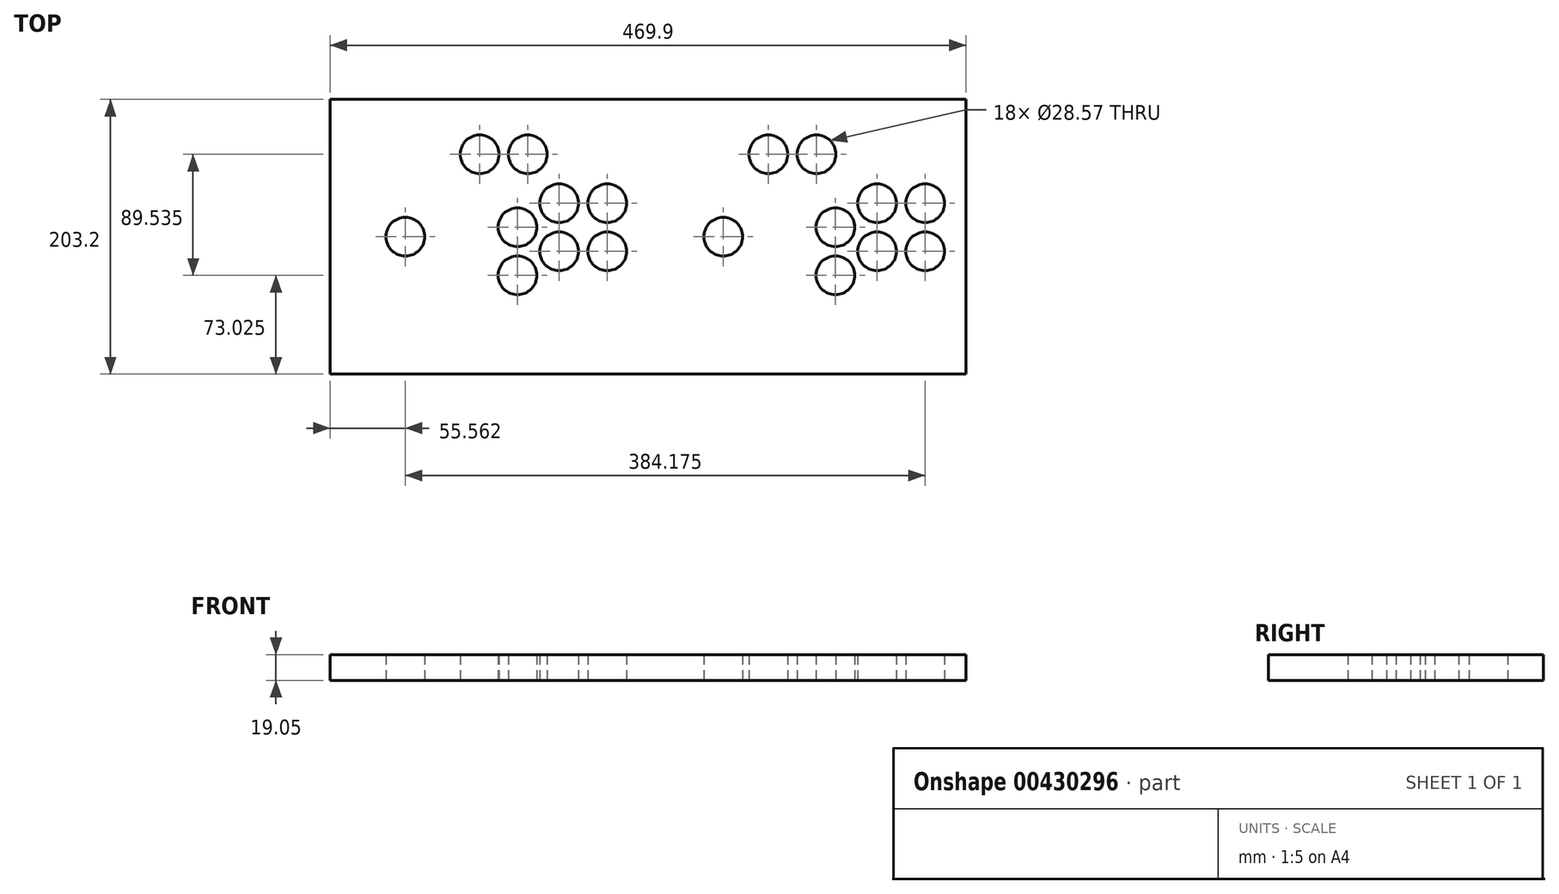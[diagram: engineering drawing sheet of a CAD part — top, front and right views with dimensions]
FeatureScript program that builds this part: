
annotation { "Feature Type Name" : "Feature", "Feature Type Description" : "" }
export const myFeature = defineFeature(function(context is Context, id is Id, definition is map)
    precondition{}
    {
        {
            var Q0;
            Q0=qCreatedBy(makeId("Top.planeOp"),FACE);
            var sketch = newSketch(context, id + "F0", { "sketchPlane" : qUnion([Q0])});
            skCircle(sketch, "E0", {"center": v(-179.39, 0) * mm, "radius": 14.29 * mm});
            skLineSegment(sketch, "E1.bottom", {"start": v(-219.08, -44.45) * mm, "end": v(-139.7, -44.45) * mm});
            skLineSegment(sketch, "E1.top", {"start": v(-219.08, 44.45) * mm, "end": v(-139.7, 44.45) * mm});
            skLineSegment(sketch, "E1.left", {"start": v(-219.08, -44.45) * mm, "end": v(-219.08, 44.45) * mm});
            skLineSegment(sketch, "E1.right", {"start": v(-139.7, -44.45) * mm, "end": v(-139.7, 44.45) * mm});
            skPoint(sketch, "E2.positionSnap0", {"position": v(-139.7, 0) * mm});
            skPoint(sketch, "E2.positionSnap1", {"position": v(-179.39, -44.45) * mm});
            skCircle(sketch, "E3", {"center": v(-96.52, -28.58) * mm, "radius": 14.29 * mm});
            skCircle(sketch, "E4", {"center": v(-96.52, 6.98) * mm, "radius": 14.29 * mm});
            skCircle(sketch, "E5", {"center": v(-30.16, 24.76) * mm, "radius": 14.29 * mm});
            skCircle(sketch, "E6", {"center": v(-65.72, -10.8) * mm, "radius": 14.29 * mm});
            skCircle(sketch, "E7", {"center": v(-65.72, 24.76) * mm, "radius": 14.29 * mm});
            skCircle(sketch, "E8", {"center": v(-30.16, -10.8) * mm, "radius": 14.29 * mm});
            skLineSegment(sketch, "E9", {"start": v(-96.52, -28.58) * mm, "end": v(-96.52, 0) * mm, "construction": true});
            skLineSegment(sketch, "E10", {"start": v(-179.39, 0) * mm, "end": v(-96.52, 0) * mm, "construction": true});
            skLineSegment(sketch, "E11", {"start": v(-96.52, -28.58) * mm, "end": v(-96.52, 6.98) * mm, "construction": true});
            skLineSegment(sketch, "E12", {"start": v(-96.52, 6.98) * mm, "end": v(-65.72, 24.76) * mm, "construction": true});
            skLineSegment(sketch, "E13", {"start": v(-65.72, 24.76) * mm, "end": v(-30.16, 24.76) * mm, "construction": true});
            skLineSegment(sketch, "E14", {"start": v(-30.16, 24.76) * mm, "end": v(-30.16, -10.8) * mm, "construction": true});
            skLineSegment(sketch, "E15", {"start": v(-65.72, 24.76) * mm, "end": v(-65.72, -10.8) * mm, "construction": true});
            skLineSegment(sketch, "E16", {"start": v(-96.52, 6.98) * mm, "end": v(-65.72, -10.8) * mm, "construction": true});
            skPoint(sketch, "E17", {"position": v(-15.87, -10.8) * mm});
            skLineSegment(sketch, "E18", {"start": v(-219.08, -44.45) * mm, "end": v(-15.87, -44.45) * mm, "construction": true});
            skPoint(sketch, "E19", {"position": v(-117.47, -44.45) * mm});
            skPoint(sketch, "E20", {"position": v(-219.08, 0) * mm});
            skLineSegment(sketch, "E21", {"start": v(-234.95, 0) * mm, "end": v(0, 0) * mm, "construction": true});
            skLineSegment(sketch, "E22", {"start": v(0, 0) * mm, "end": v(234.95, 0) * mm, "construction": true});
            skLineSegment(sketch, "E23", {"start": v(-117.47, 0) * mm, "end": v(-117.47, -104.7) * mm, "construction": true});
            skLineSegment(sketch, "E24", {"start": v(117.48, 0) * mm, "end": v(117.48, -102.15) * mm, "construction": true});
            skCircle(sketch, "E25", {"center": v(55.56, 0) * mm, "radius": 14.29 * mm});
            skLineSegment(sketch, "E26.bottom", {"start": v(15.88, -44.45) * mm, "end": v(95.25, -44.45) * mm});
            skLineSegment(sketch, "E26.top", {"start": v(15.88, 44.45) * mm, "end": v(95.25, 44.45) * mm});
            skLineSegment(sketch, "E26.left", {"start": v(15.88, -44.45) * mm, "end": v(15.88, 44.45) * mm});
            skLineSegment(sketch, "E26.right", {"start": v(95.25, -44.45) * mm, "end": v(95.25, 44.45) * mm});
            skPoint(sketch, "E27.positionSnap0", {"position": v(95.25, 0) * mm});
            skPoint(sketch, "E27.positionSnap1", {"position": v(55.56, -44.45) * mm});
            skCircle(sketch, "E28", {"center": v(138.43, -28.58) * mm, "radius": 14.29 * mm});
            skCircle(sketch, "E29", {"center": v(138.43, 6.98) * mm, "radius": 14.29 * mm});
            skCircle(sketch, "E30", {"center": v(204.79, 24.77) * mm, "radius": 14.29 * mm});
            skCircle(sketch, "E31", {"center": v(169.23, -10.8) * mm, "radius": 14.29 * mm});
            skCircle(sketch, "E32", {"center": v(169.23, 24.77) * mm, "radius": 14.29 * mm});
            skCircle(sketch, "E33", {"center": v(204.79, -10.8) * mm, "radius": 14.29 * mm});
            skLineSegment(sketch, "E34", {"start": v(138.43, -28.57) * mm, "end": v(138.43, 0) * mm, "construction": true});
            skLineSegment(sketch, "E35", {"start": v(55.56, 0) * mm, "end": v(138.43, 0) * mm, "construction": true});
            skLineSegment(sketch, "E36", {"start": v(138.43, -28.57) * mm, "end": v(138.43, 6.98) * mm, "construction": true});
            skLineSegment(sketch, "E37", {"start": v(138.43, 6.99) * mm, "end": v(169.23, 24.77) * mm, "construction": true});
            skLineSegment(sketch, "E38", {"start": v(169.23, 24.77) * mm, "end": v(204.79, 24.77) * mm, "construction": true});
            skLineSegment(sketch, "E39", {"start": v(204.79, 24.77) * mm, "end": v(204.79, -10.8) * mm, "construction": true});
            skLineSegment(sketch, "E40", {"start": v(169.23, 24.77) * mm, "end": v(169.23, -10.8) * mm, "construction": true});
            skLineSegment(sketch, "E41", {"start": v(138.43, 6.99) * mm, "end": v(169.23, -10.8) * mm, "construction": true});
            skPoint(sketch, "E42", {"position": v(219.08, -10.8) * mm});
            skLineSegment(sketch, "E43", {"start": v(15.88, -44.45) * mm, "end": v(219.08, -44.45) * mm, "construction": true});
            skPoint(sketch, "E44", {"position": v(117.48, -44.45) * mm});
            skPoint(sketch, "E45", {"position": v(15.88, 0) * mm});
            skLineSegment(sketch, "E46", {"start": v(0, -104.7) * mm, "end": v(0, 0) * mm, "construction": true});
            skCircle(sketch, "E47", {"center": v(-124.46, 60.96) * mm, "radius": 14.29 * mm});
            skLineSegment(sketch, "E48", {"start": v(0, 60.96) * mm, "end": v(88.9, 60.96) * mm, "construction": true});
            skLineSegment(sketch, "E49", {"start": v(88.9, 60.96) * mm, "end": v(124.46, 60.96) * mm, "construction": true});
            skLineSegment(sketch, "E50", {"start": v(0, 60.96) * mm, "end": v(-88.9, 60.96) * mm, "construction": true});
            skLineSegment(sketch, "E51", {"start": v(-88.9, 60.96) * mm, "end": v(-124.46, 60.96) * mm, "construction": true});
            skCircle(sketch, "E52", {"center": v(-88.9, 60.96) * mm, "radius": 14.29 * mm});
            skCircle(sketch, "E53", {"center": v(88.9, 60.96) * mm, "radius": 14.29 * mm});
            skCircle(sketch, "E54", {"center": v(124.46, 60.96) * mm, "radius": 14.29 * mm});
            skLineSegment(sketch, "E55", {"start": v(0, 0) * mm, "end": v(0, 141.88) * mm, "construction": true});
            skLineSegment(sketch, "E56.bottom", {"start": v(234.95, 101.6) * mm, "end": v(-234.95, 101.6) * mm});
            skLineSegment(sketch, "E56.top", {"start": v(234.95, -101.6) * mm, "end": v(-234.95, -101.6) * mm});
            skLineSegment(sketch, "E56.left", {"start": v(234.95, 101.6) * mm, "end": v(234.95, -101.6) * mm});
            skLineSegment(sketch, "E56.right", {"start": v(-234.95, 101.6) * mm, "end": v(-234.95, -101.6) * mm});
            skPoint(sketch, "E56.middle", {"position": v(0, 0) * mm});
            skSolve(sketch);
        }
        {
            var Q0;
            Q0=makeQuery(id+"F0.imprint","IMPRINT",FACE,{"disambiguationData":[TD([[makeQuery(id+"F0.imprint","IMPRINT",EDGE,{"derivedFrom":sQuery(id+"F0.wireOp",EDGE,"E1.bottom")}),-1.0]])]});
            var Q1;
            Q1=makeQuery(id+"F0.imprint","IMPRINT",FACE,{"disambiguationData":[TD([[makeQuery(id+"F0.imprint","IMPRINT",EDGE,{"derivedFrom":sQuery(id+"F0.wireOp",EDGE,"E0")}),-1.0]])]});
            var Q2;
            Q2=makeQuery(id+"F0.imprint","IMPRINT",FACE,{"disambiguationData":[TD([[makeQuery(id+"F0.imprint","IMPRINT",EDGE,{"derivedFrom":sQuery(id+"F0.wireOp",EDGE,"E25")}),-1.0]])]});
            extrude(context, id + "F1", {"entities" : qUnion([Q0, Q1, Q2]), "depth" : 19.05 * mm, "offsetDistance" : 25.4 * mm});
        }
    });
